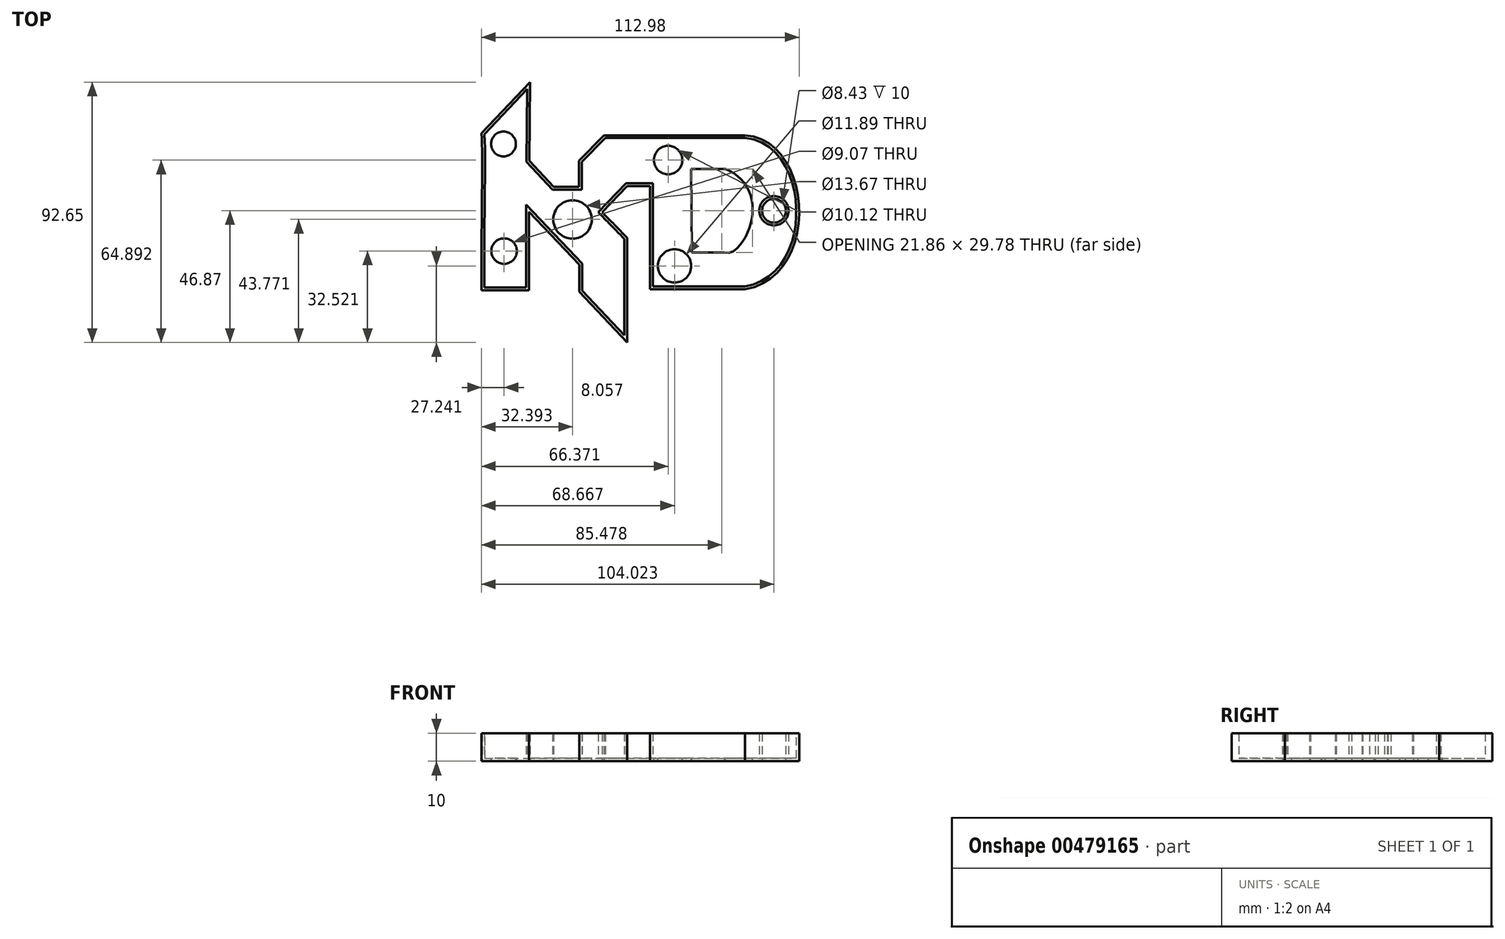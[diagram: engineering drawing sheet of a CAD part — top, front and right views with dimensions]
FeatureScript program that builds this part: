
annotation { "Feature Type Name" : "Feature", "Feature Type Description" : "" }
export const myFeature = defineFeature(function(context is Context, id is Id, definition is map)
    precondition{}
    {
        {
            var Q0;
            Q0=qCreatedBy(makeId("Top.planeOp"),FACE);
            var sketch = newSketch(context, id + "F0", { "sketchPlane" : qUnion([Q0])});
            skFitSpline(sketch, "E0", {"points": [v(-56.04, 27.58) * mm, v(-38.8, 45.78) * mm], "startDerivative": vector(17.23, 18.2) * mm, "endDerivative": vector(17.23, 18.2) * mm});
            skFitSpline(sketch, "E1", {"points": [v(-56.04, 27.58) * mm, v(-55.86, 6.37) * mm, v(-56.04, -28.33) * mm], "startDerivative": vector(2.8, -45.11) * mm, "endDerivative": vector(-0.18, -79.58) * mm});
            skFitSpline(sketch, "E2", {"points": [v(-56.04, -28.33) * mm, v(-39.15, -28.33) * mm], "startDerivative": vector(16.89, 0) * mm, "endDerivative": vector(16.89, 0) * mm});
            skFitSpline(sketch, "E3", {"points": [v(-39.15, -28.33) * mm, v(-39.15, -0.32) * mm], "startDerivative": vector(0, 28.01) * mm, "endDerivative": vector(0, 28.01) * mm});
            skFitSpline(sketch, "E4", {"points": [v(-39.15, -0.32) * mm, v(-21.17, -19.17) * mm], "startDerivative": vector(17.97, -18.85) * mm, "endDerivative": vector(17.97, -18.85) * mm});
            skFitSpline(sketch, "E5", {"points": [v(-21.17, -19.17) * mm, v(-21.17, -28.8) * mm], "startDerivative": vector(0, -9.63) * mm, "endDerivative": vector(0, -9.63) * mm});
            skFitSpline(sketch, "E6", {"points": [v(-21.17, -28.8) * mm, v(-4.2, -46.87) * mm], "startDerivative": vector(16.97, -18.07) * mm, "endDerivative": vector(16.97, -18.07) * mm});
            skFitSpline(sketch, "E7", {"points": [v(-4.2, -46.87) * mm, v(-4.2, -9.63) * mm], "startDerivative": vector(0, 37.24) * mm, "endDerivative": vector(0, 37.24) * mm});
            skFitSpline(sketch, "E8", {"points": [v(-4.2, -9.63) * mm, v(-13.08, -0.55) * mm], "startDerivative": vector(-8.55, 8.84) * mm, "endDerivative": vector(-8.55, 8.84) * mm});
            skFitSpline(sketch, "E9", {"points": [v(-13.08, -0.55) * mm, v(-4.21, 8.75) * mm], "startDerivative": vector(8.86, 9.3) * mm, "endDerivative": vector(8.86, 9.3) * mm});
            skFitSpline(sketch, "E10", {"points": [v(-4.21, 8.75) * mm, v(3.9, 8.75) * mm], "startDerivative": vector(8.12, 0) * mm, "endDerivative": vector(8.12, 0) * mm});
            skFitSpline(sketch, "E11", {"points": [v(3.9, 8.75) * mm, v(3.9, -27.97) * mm], "startDerivative": vector(0, -36.66) * mm, "endDerivative": vector(0, -36.66) * mm});
            skFitSpline(sketch, "E12", {"points": [v(3.9, -27.97) * mm, v(37.75, -27.97) * mm], "startDerivative": vector(34.61, 0) * mm, "endDerivative": vector(34.61, 0) * mm});
            skFitSpline(sketch, "E13", {"points": [v(37.75, -27.97) * mm, v(37.75, 26.86) * mm], "startDerivative": vector(80.5, 13.9) * mm, "endDerivative": vector(-72.98, 5.21) * mm});
            skFitSpline(sketch, "E14", {"points": [v(37.75, 26.86) * mm, v(-12.45, 26.86) * mm], "startDerivative": vector(-50.2, 0) * mm, "endDerivative": vector(-50.2, 0) * mm});
            skFitSpline(sketch, "E15", {"points": [v(-12.45, 26.86) * mm, v(-21.33, 17.78) * mm], "startDerivative": vector(-8.88, -9.07) * mm, "endDerivative": vector(-8.88, -9.07) * mm});
            skFitSpline(sketch, "E16", {"points": [v(-21.33, 17.78) * mm, v(-21.33, 8.5) * mm], "startDerivative": vector(0, -9.3) * mm, "endDerivative": vector(0, -9.3) * mm});
            skFitSpline(sketch, "E17", {"points": [v(-21.33, 8.5) * mm, v(-30.35, 8.5) * mm], "startDerivative": vector(-9.02, 0) * mm, "endDerivative": vector(-9.02, 0) * mm});
            skFitSpline(sketch, "E18", {"points": [v(-30.35, 8.5) * mm, v(-38.99, 17.78) * mm], "startDerivative": vector(-8.64, 9.3) * mm, "endDerivative": vector(-8.64, 9.3) * mm});
            skFitSpline(sketch, "E19", {"points": [v(-38.99, 17.78) * mm, v(-38.8, 45.78) * mm], "startDerivative": vector(0.18, 28) * mm, "endDerivative": vector(0.18, 28) * mm});
            skFitSpline(sketch, "E20", {"points": [v(19.51, 13.89) * mm, v(19.74, -13.89) * mm], "startDerivative": vector(0.23, -27.78) * mm, "endDerivative": vector(0.23, -27.78) * mm});
            skFitSpline(sketch, "E21", {"points": [v(19.51, 13.89) * mm, v(30.53, 13.89) * mm], "startDerivative": vector(11.02, 0) * mm, "endDerivative": vector(11.02, 0) * mm});
            skFitSpline(sketch, "E22", {"points": [v(19.74, -13.89) * mm, v(30.53, -13.89) * mm], "startDerivative": vector(10.8, 0) * mm, "endDerivative": vector(10.8, 0) * mm});
            skFitSpline(sketch, "E23", {"points": [v(30.53, 13.89) * mm, v(30.53, -13.89) * mm], "startDerivative": vector(50.97, -22.04) * mm, "endDerivative": vector(-15.84, 7.58) * mm});
            skCircle(sketch, "E24", {"center": v(-48.21, 23.76) * mm, "radius": 3.41 * mm});
            skCircle(sketch, "E25", {"center": v(-47.98, -14.35) * mm, "radius": 3.54 * mm});
            skCircle(sketch, "E26", {"center": v(-23.65, -3.1) * mm, "radius": 5.83 * mm});
            skCircle(sketch, "E27", {"center": v(10.33, 18.02) * mm, "radius": 4.06 * mm});
            skCircle(sketch, "E28", {"center": v(12.63, -19.63) * mm, "radius": 4.94 * mm});
            skCircle(sketch, "E29", {"center": v(47.98, 0) * mm, "radius": 4.21 * mm});
            skSolve(sketch);
        }
        {
            var Q0;
            Q0=makeQuery(id+"F0.imprint","IMPRINT",FACE,{"disambiguationData":[TD([[makeQuery(id+"F0.imprint","IMPRINT",EDGE,{"derivedFrom":sQuery(id+"F0.wireOp",EDGE,"E0")}),-1.0]])]});
            extrude(context, id + "F1", {"entities" : qUnion([Q0]), "depth" : 10 * mm});
        }
        {
            var Q0;
            Q0=makeQuery(id+"F1.opExtrude","CAP_FACE",FACE,{"disambiguationData":[OSD([sQuery(id+"F0.wireOp",EDGE,"E0"),sQuery(id+"F0.wireOp",EDGE,"E1"),sQuery(id+"F0.wireOp",EDGE,"E2"),sQuery(id+"F0.wireOp",EDGE,"E3"),sQuery(id+"F0.wireOp",EDGE,"E4"),sQuery(id+"F0.wireOp",EDGE,"E5"),sQuery(id+"F0.wireOp",EDGE,"E6"),sQuery(id+"F0.wireOp",EDGE,"E7"),sQuery(id+"F0.wireOp",EDGE,"E8"),sQuery(id+"F0.wireOp",EDGE,"E9"),sQuery(id+"F0.wireOp",EDGE,"E10"),sQuery(id+"F0.wireOp",EDGE,"E11"),sQuery(id+"F0.wireOp",EDGE,"E12"),sQuery(id+"F0.wireOp",EDGE,"E13"),sQuery(id+"F0.wireOp",EDGE,"E14"),sQuery(id+"F0.wireOp",EDGE,"E15"),sQuery(id+"F0.wireOp",EDGE,"E16"),sQuery(id+"F0.wireOp",EDGE,"E17"),sQuery(id+"F0.wireOp",EDGE,"E18"),sQuery(id+"F0.wireOp",EDGE,"E19"),sQuery(id+"F0.wireOp",EDGE,"E20"),sQuery(id+"F0.wireOp",EDGE,"E21"),sQuery(id+"F0.wireOp",EDGE,"E22"),sQuery(id+"F0.wireOp",EDGE,"E23")])],"isStart":false});
            shell(context, id + "F2", {"entities" : qUnion([Q0]), "thickness" : 1 * mm});
        }
        {
            var Q0;
            {var subQ0=sQuery(id+"F0.wireOp",EDGE,"E29");var subQ1=sQuery(id+"F0.wireOp",EDGE,"E28");var subQ2=sQuery(id+"F0.wireOp",EDGE,"E27");var subQ3=sQuery(id+"F0.wireOp",EDGE,"E26");var subQ4=sQuery(id+"F0.wireOp",EDGE,"E25");var subQ5=sQuery(id+"F0.wireOp",EDGE,"E24");var subQ6=sQuery(id+"F0.wireOp",EDGE,"E23");var subQ7=sQuery(id+"F0.wireOp",EDGE,"E22");var subQ8=sQuery(id+"F0.wireOp",EDGE,"E21");var subQ9=sQuery(id+"F0.wireOp",EDGE,"E20");var subQ10=sQuery(id+"F0.wireOp",EDGE,"E19");var subQ11=sQuery(id+"F0.wireOp",EDGE,"E18");var subQ12=sQuery(id+"F0.wireOp",EDGE,"E17");var subQ13=sQuery(id+"F0.wireOp",EDGE,"E16");var subQ14=sQuery(id+"F0.wireOp",EDGE,"E15");var subQ15=sQuery(id+"F0.wireOp",EDGE,"E14");var subQ16=sQuery(id+"F0.wireOp",EDGE,"E13");var subQ17=sQuery(id+"F0.wireOp",EDGE,"E12");var subQ18=sQuery(id+"F0.wireOp",EDGE,"E11");var subQ19=sQuery(id+"F0.wireOp",EDGE,"E10");var subQ20=sQuery(id+"F0.wireOp",EDGE,"E9");var subQ21=sQuery(id+"F0.wireOp",EDGE,"E8");var subQ22=sQuery(id+"F0.wireOp",EDGE,"E7");var subQ23=sQuery(id+"F0.wireOp",EDGE,"E6");var subQ24=sQuery(id+"F0.wireOp",EDGE,"E5");var subQ25=sQuery(id+"F0.wireOp",EDGE,"E4");var subQ26=sQuery(id+"F0.wireOp",EDGE,"E3");var subQ27=sQuery(id+"F0.wireOp",EDGE,"E2");var subQ28=sQuery(id+"F0.wireOp",EDGE,"E1");var subQ29=sQuery(id+"F0.wireOp",EDGE,"E0");Q0=makeQuery(id+"F2.opShell","OFFSET_FACE",FACE,{"disambiguationData":[OSD([subQ29,subQ28,subQ27,subQ26,subQ25,subQ24,subQ23,subQ22,subQ21,subQ20,subQ19,subQ18,subQ17,subQ16,subQ15,subQ14,subQ13,subQ12,subQ11,subQ10,subQ9,subQ8,subQ7,subQ6,subQ5,subQ4,subQ3,subQ2,subQ1,subQ0]),TDD([makeQuery(id+"F1.opExtrude","CAP_FACE",FACE,{"disambiguationData":[OSD([subQ29,subQ28,subQ27,subQ26,subQ25,subQ24,subQ23,subQ22,subQ21,subQ20,subQ19,subQ18,subQ17,subQ16,subQ15,subQ14,subQ13,subQ12,subQ11,subQ10,subQ9,subQ8,subQ7,subQ6,subQ5,subQ4,subQ3,subQ2,subQ1,subQ0])],"isStart":false})]),OD(2.0)]});}
            var Q1;
            {var subQ0=sQuery(id+"F0.wireOp",EDGE,"E29");var subQ1=sQuery(id+"F0.wireOp",EDGE,"E28");var subQ2=sQuery(id+"F0.wireOp",EDGE,"E27");var subQ3=sQuery(id+"F0.wireOp",EDGE,"E26");var subQ4=sQuery(id+"F0.wireOp",EDGE,"E25");var subQ5=sQuery(id+"F0.wireOp",EDGE,"E24");var subQ6=sQuery(id+"F0.wireOp",EDGE,"E23");var subQ7=sQuery(id+"F0.wireOp",EDGE,"E22");var subQ8=sQuery(id+"F0.wireOp",EDGE,"E21");var subQ9=sQuery(id+"F0.wireOp",EDGE,"E20");var subQ10=sQuery(id+"F0.wireOp",EDGE,"E19");var subQ11=sQuery(id+"F0.wireOp",EDGE,"E18");var subQ12=sQuery(id+"F0.wireOp",EDGE,"E17");var subQ13=sQuery(id+"F0.wireOp",EDGE,"E16");var subQ14=sQuery(id+"F0.wireOp",EDGE,"E15");var subQ15=sQuery(id+"F0.wireOp",EDGE,"E14");var subQ16=sQuery(id+"F0.wireOp",EDGE,"E13");var subQ17=sQuery(id+"F0.wireOp",EDGE,"E12");var subQ18=sQuery(id+"F0.wireOp",EDGE,"E11");var subQ19=sQuery(id+"F0.wireOp",EDGE,"E10");var subQ20=sQuery(id+"F0.wireOp",EDGE,"E9");var subQ21=sQuery(id+"F0.wireOp",EDGE,"E8");var subQ22=sQuery(id+"F0.wireOp",EDGE,"E7");var subQ23=sQuery(id+"F0.wireOp",EDGE,"E6");var subQ24=sQuery(id+"F0.wireOp",EDGE,"E5");var subQ25=sQuery(id+"F0.wireOp",EDGE,"E4");var subQ26=sQuery(id+"F0.wireOp",EDGE,"E3");var subQ27=sQuery(id+"F0.wireOp",EDGE,"E2");var subQ28=sQuery(id+"F0.wireOp",EDGE,"E1");var subQ29=sQuery(id+"F0.wireOp",EDGE,"E0");Q1=makeQuery(id+"F2.opShell","OFFSET_FACE",FACE,{"disambiguationData":[OSD([subQ29,subQ28,subQ27,subQ26,subQ25,subQ24,subQ23,subQ22,subQ21,subQ20,subQ19,subQ18,subQ17,subQ16,subQ15,subQ14,subQ13,subQ12,subQ11,subQ10,subQ9,subQ8,subQ7,subQ6,subQ5,subQ4,subQ3,subQ2,subQ1,subQ0]),TDD([makeQuery(id+"F1.opExtrude","CAP_FACE",FACE,{"disambiguationData":[OSD([subQ29,subQ28,subQ27,subQ26,subQ25,subQ24,subQ23,subQ22,subQ21,subQ20,subQ19,subQ18,subQ17,subQ16,subQ15,subQ14,subQ13,subQ12,subQ11,subQ10,subQ9,subQ8,subQ7,subQ6,subQ5,subQ4,subQ3,subQ2,subQ1,subQ0])],"isStart":false})]),OD(3.0)]});}
            var Q2;
            {var subQ0=sQuery(id+"F0.wireOp",EDGE,"E29");var subQ1=sQuery(id+"F0.wireOp",EDGE,"E28");var subQ2=sQuery(id+"F0.wireOp",EDGE,"E27");var subQ3=sQuery(id+"F0.wireOp",EDGE,"E26");var subQ4=sQuery(id+"F0.wireOp",EDGE,"E25");var subQ5=sQuery(id+"F0.wireOp",EDGE,"E24");var subQ6=sQuery(id+"F0.wireOp",EDGE,"E23");var subQ7=sQuery(id+"F0.wireOp",EDGE,"E22");var subQ8=sQuery(id+"F0.wireOp",EDGE,"E21");var subQ9=sQuery(id+"F0.wireOp",EDGE,"E20");var subQ10=sQuery(id+"F0.wireOp",EDGE,"E19");var subQ11=sQuery(id+"F0.wireOp",EDGE,"E18");var subQ12=sQuery(id+"F0.wireOp",EDGE,"E17");var subQ13=sQuery(id+"F0.wireOp",EDGE,"E16");var subQ14=sQuery(id+"F0.wireOp",EDGE,"E15");var subQ15=sQuery(id+"F0.wireOp",EDGE,"E14");var subQ16=sQuery(id+"F0.wireOp",EDGE,"E13");var subQ17=sQuery(id+"F0.wireOp",EDGE,"E12");var subQ18=sQuery(id+"F0.wireOp",EDGE,"E11");var subQ19=sQuery(id+"F0.wireOp",EDGE,"E10");var subQ20=sQuery(id+"F0.wireOp",EDGE,"E9");var subQ21=sQuery(id+"F0.wireOp",EDGE,"E8");var subQ22=sQuery(id+"F0.wireOp",EDGE,"E7");var subQ23=sQuery(id+"F0.wireOp",EDGE,"E6");var subQ24=sQuery(id+"F0.wireOp",EDGE,"E5");var subQ25=sQuery(id+"F0.wireOp",EDGE,"E4");var subQ26=sQuery(id+"F0.wireOp",EDGE,"E3");var subQ27=sQuery(id+"F0.wireOp",EDGE,"E2");var subQ28=sQuery(id+"F0.wireOp",EDGE,"E1");var subQ29=sQuery(id+"F0.wireOp",EDGE,"E0");Q2=makeQuery(id+"F2.opShell","OFFSET_FACE",FACE,{"disambiguationData":[OSD([subQ29,subQ28,subQ27,subQ26,subQ25,subQ24,subQ23,subQ22,subQ21,subQ20,subQ19,subQ18,subQ17,subQ16,subQ15,subQ14,subQ13,subQ12,subQ11,subQ10,subQ9,subQ8,subQ7,subQ6,subQ5,subQ4,subQ3,subQ2,subQ1,subQ0]),TDD([makeQuery(id+"F1.opExtrude","CAP_FACE",FACE,{"disambiguationData":[OSD([subQ29,subQ28,subQ27,subQ26,subQ25,subQ24,subQ23,subQ22,subQ21,subQ20,subQ19,subQ18,subQ17,subQ16,subQ15,subQ14,subQ13,subQ12,subQ11,subQ10,subQ9,subQ8,subQ7,subQ6,subQ5,subQ4,subQ3,subQ2,subQ1,subQ0])],"isStart":false})]),OD(1.0)]});}
            var Q3;
            {var subQ0=sQuery(id+"F0.wireOp",EDGE,"E29");var subQ1=sQuery(id+"F0.wireOp",EDGE,"E28");var subQ2=sQuery(id+"F0.wireOp",EDGE,"E27");var subQ3=sQuery(id+"F0.wireOp",EDGE,"E26");var subQ4=sQuery(id+"F0.wireOp",EDGE,"E25");var subQ5=sQuery(id+"F0.wireOp",EDGE,"E24");var subQ6=sQuery(id+"F0.wireOp",EDGE,"E23");var subQ7=sQuery(id+"F0.wireOp",EDGE,"E22");var subQ8=sQuery(id+"F0.wireOp",EDGE,"E21");var subQ9=sQuery(id+"F0.wireOp",EDGE,"E20");var subQ10=sQuery(id+"F0.wireOp",EDGE,"E19");var subQ11=sQuery(id+"F0.wireOp",EDGE,"E18");var subQ12=sQuery(id+"F0.wireOp",EDGE,"E17");var subQ13=sQuery(id+"F0.wireOp",EDGE,"E16");var subQ14=sQuery(id+"F0.wireOp",EDGE,"E15");var subQ15=sQuery(id+"F0.wireOp",EDGE,"E14");var subQ16=sQuery(id+"F0.wireOp",EDGE,"E13");var subQ17=sQuery(id+"F0.wireOp",EDGE,"E12");var subQ18=sQuery(id+"F0.wireOp",EDGE,"E11");var subQ19=sQuery(id+"F0.wireOp",EDGE,"E10");var subQ20=sQuery(id+"F0.wireOp",EDGE,"E9");var subQ21=sQuery(id+"F0.wireOp",EDGE,"E8");var subQ22=sQuery(id+"F0.wireOp",EDGE,"E7");var subQ23=sQuery(id+"F0.wireOp",EDGE,"E6");var subQ24=sQuery(id+"F0.wireOp",EDGE,"E5");var subQ25=sQuery(id+"F0.wireOp",EDGE,"E4");var subQ26=sQuery(id+"F0.wireOp",EDGE,"E3");var subQ27=sQuery(id+"F0.wireOp",EDGE,"E2");var subQ28=sQuery(id+"F0.wireOp",EDGE,"E1");var subQ29=sQuery(id+"F0.wireOp",EDGE,"E0");Q3=makeQuery(id+"F2.opShell","OFFSET_FACE",FACE,{"disambiguationData":[OSD([subQ29,subQ28,subQ27,subQ26,subQ25,subQ24,subQ23,subQ22,subQ21,subQ20,subQ19,subQ18,subQ17,subQ16,subQ15,subQ14,subQ13,subQ12,subQ11,subQ10,subQ9,subQ8,subQ7,subQ6,subQ5,subQ4,subQ3,subQ2,subQ1,subQ0]),TDD([makeQuery(id+"F1.opExtrude","CAP_FACE",FACE,{"disambiguationData":[OSD([subQ29,subQ28,subQ27,subQ26,subQ25,subQ24,subQ23,subQ22,subQ21,subQ20,subQ19,subQ18,subQ17,subQ16,subQ15,subQ14,subQ13,subQ12,subQ11,subQ10,subQ9,subQ8,subQ7,subQ6,subQ5,subQ4,subQ3,subQ2,subQ1,subQ0])],"isStart":false})]),OD(4.0)]});}
            var Q4;
            {var subQ0=sQuery(id+"F0.wireOp",EDGE,"E29");var subQ1=sQuery(id+"F0.wireOp",EDGE,"E28");var subQ2=sQuery(id+"F0.wireOp",EDGE,"E27");var subQ3=sQuery(id+"F0.wireOp",EDGE,"E26");var subQ4=sQuery(id+"F0.wireOp",EDGE,"E25");var subQ5=sQuery(id+"F0.wireOp",EDGE,"E24");var subQ6=sQuery(id+"F0.wireOp",EDGE,"E23");var subQ7=sQuery(id+"F0.wireOp",EDGE,"E22");var subQ8=sQuery(id+"F0.wireOp",EDGE,"E21");var subQ9=sQuery(id+"F0.wireOp",EDGE,"E20");var subQ10=sQuery(id+"F0.wireOp",EDGE,"E19");var subQ11=sQuery(id+"F0.wireOp",EDGE,"E18");var subQ12=sQuery(id+"F0.wireOp",EDGE,"E17");var subQ13=sQuery(id+"F0.wireOp",EDGE,"E16");var subQ14=sQuery(id+"F0.wireOp",EDGE,"E15");var subQ15=sQuery(id+"F0.wireOp",EDGE,"E14");var subQ16=sQuery(id+"F0.wireOp",EDGE,"E13");var subQ17=sQuery(id+"F0.wireOp",EDGE,"E12");var subQ18=sQuery(id+"F0.wireOp",EDGE,"E11");var subQ19=sQuery(id+"F0.wireOp",EDGE,"E10");var subQ20=sQuery(id+"F0.wireOp",EDGE,"E9");var subQ21=sQuery(id+"F0.wireOp",EDGE,"E8");var subQ22=sQuery(id+"F0.wireOp",EDGE,"E7");var subQ23=sQuery(id+"F0.wireOp",EDGE,"E6");var subQ24=sQuery(id+"F0.wireOp",EDGE,"E5");var subQ25=sQuery(id+"F0.wireOp",EDGE,"E4");var subQ26=sQuery(id+"F0.wireOp",EDGE,"E3");var subQ27=sQuery(id+"F0.wireOp",EDGE,"E2");var subQ28=sQuery(id+"F0.wireOp",EDGE,"E1");var subQ29=sQuery(id+"F0.wireOp",EDGE,"E0");Q4=makeQuery(id+"F2.opShell","OFFSET_FACE",FACE,{"disambiguationData":[OSD([subQ29,subQ28,subQ27,subQ26,subQ25,subQ24,subQ23,subQ22,subQ21,subQ20,subQ19,subQ18,subQ17,subQ16,subQ15,subQ14,subQ13,subQ12,subQ11,subQ10,subQ9,subQ8,subQ7,subQ6,subQ5,subQ4,subQ3,subQ2,subQ1,subQ0]),TDD([makeQuery(id+"F1.opExtrude","CAP_FACE",FACE,{"disambiguationData":[OSD([subQ29,subQ28,subQ27,subQ26,subQ25,subQ24,subQ23,subQ22,subQ21,subQ20,subQ19,subQ18,subQ17,subQ16,subQ15,subQ14,subQ13,subQ12,subQ11,subQ10,subQ9,subQ8,subQ7,subQ6,subQ5,subQ4,subQ3,subQ2,subQ1,subQ0])],"isStart":false})]),OD(5.0)]});}
            var Q5;
            {var subQ0=sQuery(id+"F0.wireOp",EDGE,"E29");var subQ1=sQuery(id+"F0.wireOp",EDGE,"E28");var subQ2=sQuery(id+"F0.wireOp",EDGE,"E27");var subQ3=sQuery(id+"F0.wireOp",EDGE,"E26");var subQ4=sQuery(id+"F0.wireOp",EDGE,"E25");var subQ5=sQuery(id+"F0.wireOp",EDGE,"E24");var subQ6=sQuery(id+"F0.wireOp",EDGE,"E23");var subQ7=sQuery(id+"F0.wireOp",EDGE,"E22");var subQ8=sQuery(id+"F0.wireOp",EDGE,"E21");var subQ9=sQuery(id+"F0.wireOp",EDGE,"E20");var subQ10=sQuery(id+"F0.wireOp",EDGE,"E19");var subQ11=sQuery(id+"F0.wireOp",EDGE,"E18");var subQ12=sQuery(id+"F0.wireOp",EDGE,"E17");var subQ13=sQuery(id+"F0.wireOp",EDGE,"E16");var subQ14=sQuery(id+"F0.wireOp",EDGE,"E15");var subQ15=sQuery(id+"F0.wireOp",EDGE,"E14");var subQ16=sQuery(id+"F0.wireOp",EDGE,"E13");var subQ17=sQuery(id+"F0.wireOp",EDGE,"E12");var subQ18=sQuery(id+"F0.wireOp",EDGE,"E11");var subQ19=sQuery(id+"F0.wireOp",EDGE,"E10");var subQ20=sQuery(id+"F0.wireOp",EDGE,"E9");var subQ21=sQuery(id+"F0.wireOp",EDGE,"E8");var subQ22=sQuery(id+"F0.wireOp",EDGE,"E7");var subQ23=sQuery(id+"F0.wireOp",EDGE,"E6");var subQ24=sQuery(id+"F0.wireOp",EDGE,"E5");var subQ25=sQuery(id+"F0.wireOp",EDGE,"E4");var subQ26=sQuery(id+"F0.wireOp",EDGE,"E3");var subQ27=sQuery(id+"F0.wireOp",EDGE,"E2");var subQ28=sQuery(id+"F0.wireOp",EDGE,"E1");var subQ29=sQuery(id+"F0.wireOp",EDGE,"E0");Q5=makeQuery(id+"F2.opShell","OFFSET_FACE",FACE,{"disambiguationData":[OSD([subQ29,subQ28,subQ27,subQ26,subQ25,subQ24,subQ23,subQ22,subQ21,subQ20,subQ19,subQ18,subQ17,subQ16,subQ15,subQ14,subQ13,subQ12,subQ11,subQ10,subQ9,subQ8,subQ7,subQ6,subQ5,subQ4,subQ3,subQ2,subQ1,subQ0]),TDD([makeQuery(id+"F1.opExtrude","CAP_FACE",FACE,{"disambiguationData":[OSD([subQ29,subQ28,subQ27,subQ26,subQ25,subQ24,subQ23,subQ22,subQ21,subQ20,subQ19,subQ18,subQ17,subQ16,subQ15,subQ14,subQ13,subQ12,subQ11,subQ10,subQ9,subQ8,subQ7,subQ6,subQ5,subQ4,subQ3,subQ2,subQ1,subQ0])],"isStart":false})]),OD(6.0)]});}
            extrude(context, id + "F3", {"entities" : qUnion([Q0, Q1, Q2, Q3, Q4, Q5]), "operationType" : NewBodyOperationType.REMOVE, "oppositeDirection" : true, "depth" : 25 * mm});
        }
    });
